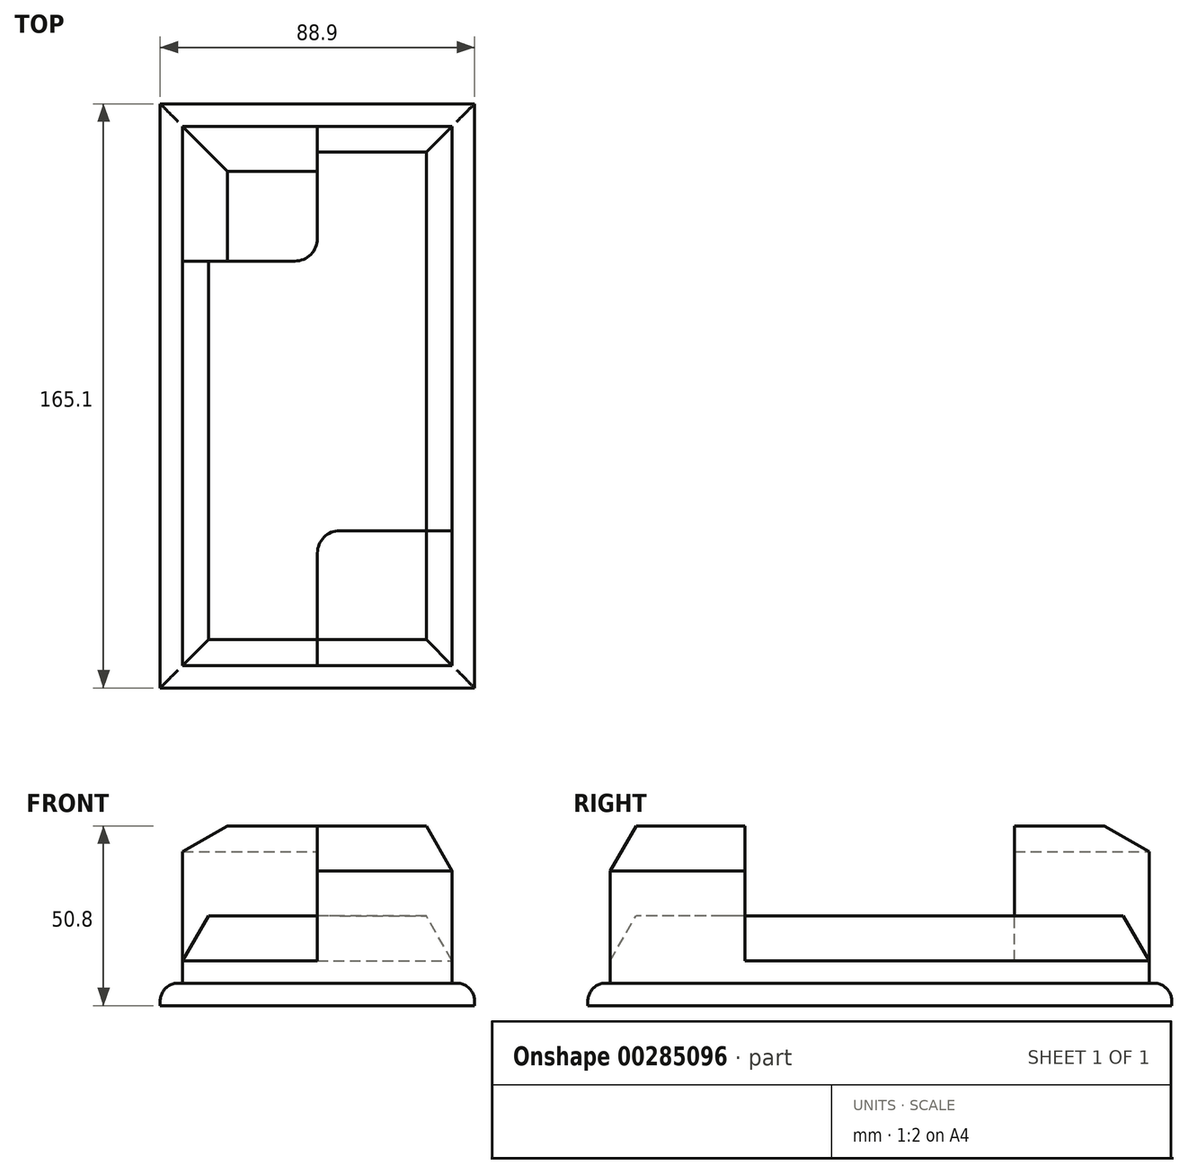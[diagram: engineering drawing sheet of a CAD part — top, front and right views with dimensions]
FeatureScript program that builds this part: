
annotation { "Feature Type Name" : "Feature", "Feature Type Description" : "" }
export const myFeature = defineFeature(function(context is Context, id is Id, definition is map)
    precondition{}
    {
        {
            var Q0;
            Q0=qCreatedBy(makeId("Top.planeOp"),FACE);
            var sketch = newSketch(context, id + "F0", { "sketchPlane" : qUnion([Q0])});
            skLineSegment(sketch, "E0", {"start": v(-51.3, 98.25) * mm, "end": v(-51.3, -54.15) * mm});
            skLineSegment(sketch, "E1", {"start": v(24.9, -54.15) * mm, "end": v(-51.3, -54.15) * mm});
            skLineSegment(sketch, "E2", {"start": v(24.9, -54.15) * mm, "end": v(24.9, 98.25) * mm});
            skLineSegment(sketch, "E3", {"start": v(24.9, 98.25) * mm, "end": v(-51.3, 98.25) * mm});
            skLineSegment(sketch, "E4.0", {"start": v(31.25, 104.6) * mm, "end": v(-57.65, 104.6) * mm});
            skLineSegment(sketch, "E4.1", {"start": v(31.25, -60.5) * mm, "end": v(31.25, 104.6) * mm});
            skLineSegment(sketch, "E4.2", {"start": v(31.25, -60.5) * mm, "end": v(-57.65, -60.5) * mm});
            skLineSegment(sketch, "E4.3", {"start": v(-57.65, 104.6) * mm, "end": v(-57.65, -60.5) * mm});
            skArc(sketch, "E5", {"start": v(-19.55, 60.15) * mm, "mid": v(-15.06, 62) * mm, "end": v(-13.2, 66.5) * mm});
            skArc(sketch, "E6", {"start": v(-6.85, -16.05) * mm, "mid": v(-11.34, -17.91) * mm, "end": v(-13.2, -22.4) * mm});
            skLineSegment(sketch, "E7", {"start": v(-6.85, -16.05) * mm, "end": v(24.9, -16.05) * mm});
            skLineSegment(sketch, "E8", {"start": v(-13.2, -22.4) * mm, "end": v(-13.2, -54.15) * mm});
            skLineSegment(sketch, "E9", {"start": v(-13.2, 66.5) * mm, "end": v(-13.2, 98.25) * mm});
            skLineSegment(sketch, "E10", {"start": v(-19.55, 60.15) * mm, "end": v(-51.3, 60.15) * mm});
            skSolve(sketch);
        }
        {
            var Q0;
            Q0=makeQuery(id+"F0.imprint","IMPRINT",FACE,{"disambiguationData":[TD([[makeQuery(id+"F0.imprint","IMPRINT",EDGE,{"derivedFrom":sQuery(id+"F0.wireOp",EDGE,"E5")}),-1.0]])]});
            extrude(context, id + "F1", {"entities" : qUnion([Q0]), "depth" : 25.4 * mm});
        }
        {
            var Q0;
            Q0=makeQuery(id+"F0.imprint","IMPRINT",FACE,{"disambiguationData":[TD([[makeQuery(id+"F0.imprint","IMPRINT",EDGE,{"derivedFrom":sQuery(id+"F0.wireOp",EDGE,"E5")}),1.0]])]});
            var Q1;
            Q1=makeQuery(id+"F0.imprint","IMPRINT",FACE,{"disambiguationData":[TD([[makeQuery(id+"F0.imprint","IMPRINT",EDGE,{"derivedFrom":sQuery(id+"F0.wireOp",EDGE,"E6")}),1.0]])]});
            extrude(context, id + "F2", {"entities" : qUnion([Q0, Q1]), "operationType" : NewBodyOperationType.ADD, "depth" : 50.8 * mm});
        }
        {
            var Q0;
            Q0=makeQuery(id+"F0.imprint","IMPRINT",FACE,{"disambiguationData":[TD([[makeQuery(id+"F0.imprint","IMPRINT",EDGE,{"derivedFrom":sQuery(id+"F0.wireOp",EDGE,"E4.0")}),1.0]])]});
            extrude(context, id + "F3", {"entities" : qUnion([Q0]), "operationType" : NewBodyOperationType.ADD, "depth" : 6.35 * mm});
        }
        {
            var Q0;
            Q0=makeQuery(id+"F3.opExtrude","CAP_EDGE",EDGE,{"disambiguationData":[OSD([sQuery(id+"F0.wireOp",EDGE,"E4.1")])],"isStart":false});
            var Q1;
            Q1=makeQuery(id+"F3.opExtrude","CAP_EDGE",EDGE,{"disambiguationData":[OSD([sQuery(id+"F0.wireOp",EDGE,"E4.2")])],"isStart":false});
            var Q2;
            Q2=makeQuery(id+"F3.opExtrude","CAP_EDGE",EDGE,{"disambiguationData":[OSD([sQuery(id+"F0.wireOp",EDGE,"E4.3")])],"isStart":false});
            var Q3;
            Q3=makeQuery(id+"F3.opExtrude","CAP_EDGE",EDGE,{"disambiguationData":[OSD([sQuery(id+"F0.wireOp",EDGE,"E4.0")])],"isStart":false});
            fillet(context, id + "F4", {"entities" : qUnion([Q0, Q1, Q2, Q3]), "radius" : 5.08 * mm, "tangentPropagation" : true, "allowEdgeOverflow" : false});
        }
        {
            var Q0;
            Q0=makeQuery(id+"F1.opExtrude","CAP_EDGE",EDGE,{"disambiguationData":[OSD([sQuery(id+"F0.wireOp",EDGE,"E2")])],"isStart":false});
            var Q1;
            Q1=makeQuery(id+"F1.opExtrude","CAP_EDGE",EDGE,{"disambiguationData":[OSD([sQuery(id+"F0.wireOp",EDGE,"E3")])],"isStart":false});
            var Q2;
            Q2=makeQuery(id+"F1.opExtrude","CAP_EDGE",EDGE,{"disambiguationData":[OSD([sQuery(id+"F0.wireOp",EDGE,"E0")])],"isStart":false});
            var Q3;
            Q3=makeQuery(id+"F1.opExtrude","CAP_EDGE",EDGE,{"disambiguationData":[OSD([sQuery(id+"F0.wireOp",EDGE,"E1")])],"isStart":false});
            chamfer(context, id + "F5", {"entities" : qUnion([Q0, Q1, Q2, Q3]), "chamferType" : ChamferType.OFFSET_ANGLE, "width" : 12.7 * mm, "oppositeDirection" : true, "angle" : 30 * degree, "tangentPropagation" : true});
        }
        {
            var Q0;
            Q0=makeQuery(id+"F2.opExtrude","CAP_EDGE",EDGE,{"disambiguationData":[OSD([sQuery(id+"F0.wireOp",EDGE,"E1")])],"isStart":false});
            var Q1;
            Q1=makeQuery(id+"F2.opExtrude","CAP_EDGE",EDGE,{"disambiguationData":[OSD([sQuery(id+"F0.wireOp",EDGE,"E2")])],"isStart":false});
            var Q2;
            Q2=makeQuery(id+"F2.opExtrude","CAP_EDGE",EDGE,{"disambiguationData":[OSD([sQuery(id+"F0.wireOp",EDGE,"E0")])],"isStart":false});
            var Q3;
            Q3=makeQuery(id+"F2.opExtrude","CAP_EDGE",EDGE,{"disambiguationData":[OSD([sQuery(id+"F0.wireOp",EDGE,"E3")])],"isStart":false});
            chamfer(context, id + "F6", {"entities" : qUnion([Q0, Q1, Q2, Q3]), "chamferType" : ChamferType.OFFSET_ANGLE, "width" : 12.7 * mm, "oppositeDirection" : false, "angle" : 30 * degree, "tangentPropagation" : true});
        }
    });
